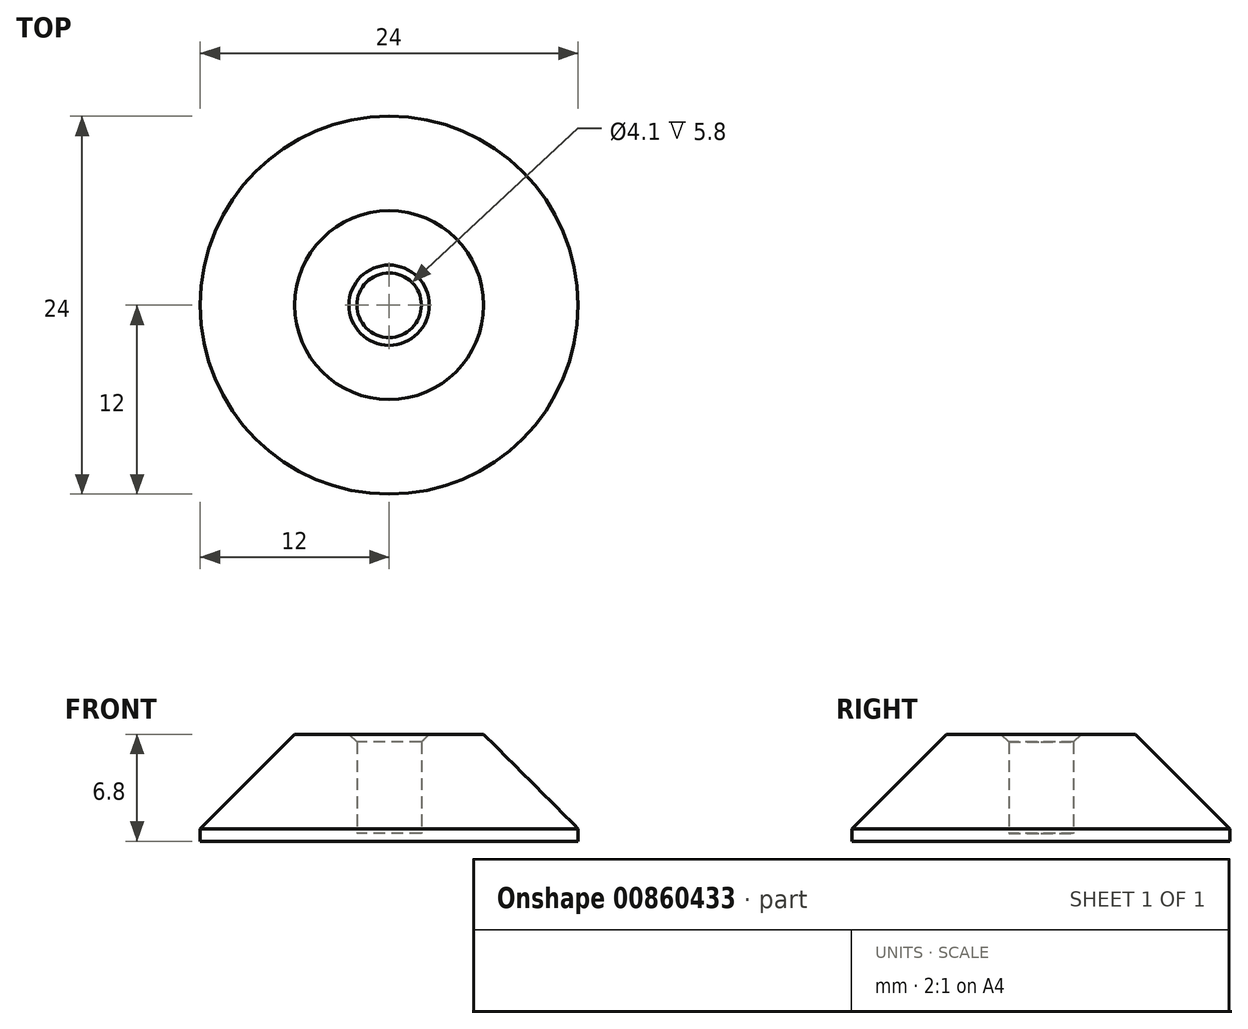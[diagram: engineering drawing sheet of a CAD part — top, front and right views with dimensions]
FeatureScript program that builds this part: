
annotation { "Feature Type Name" : "Feature", "Feature Type Description" : "" }
export const myFeature = defineFeature(function(context is Context, id is Id, definition is map)
    precondition{}
    {
        {
            var Q0;
            Q0=qCreatedBy(makeId("Top.planeOp"),FACE);
            var sketch = newSketch(context, id + "F0", { "sketchPlane" : qUnion([Q0])});
            skCircle(sketch, "E0", {"center": v(0, 0) * mm, "radius": 12 * mm});
            skCircle(sketch, "E1", {"center": v(0, 0) * mm, "radius": 2.05 * mm});
            skSolve(sketch);
        }
        {
            var Q0;
            Q0=makeQuery(id+"F0.imprint","IMPRINT",FACE,{"disambiguationData":[TD([[makeQuery(id+"F0.imprint","IMPRINT",EDGE,{"derivedFrom":sQuery(id+"F0.wireOp",EDGE,"E0")}),1.0]])]});
            extrude(context, id + "F1", {"entities" : qUnion([Q0]), "depth" : 6.8 * mm, "offsetDistance" : 25 * mm});
        }
        {
            var Q0;
            Q0=makeQuery(id+"F0.imprint","IMPRINT",FACE,{"disambiguationData":[TD([[makeQuery(id+"F0.imprint","IMPRINT",EDGE,{"derivedFrom":sQuery(id+"F0.wireOp",EDGE,"E1")}),1.0]])]});
            extrude(context, id + "F2", {"entities" : qUnion([Q0]), "operationType" : NewBodyOperationType.ADD, "depth" : 0.5 * mm, "offsetDistance" : 25 * mm});
        }
        {
            var Q0;
            Q0=makeQuery(id+"F1.opExtrude","CAP_EDGE",EDGE,{"disambiguationData":[OSD([sQuery(id+"F0.wireOp",EDGE,"E1")])],"isStart":false});
            chamfer(context, id + "F3", {"entities" : qUnion([Q0]), "width" : 0.5 * mm, "tangentPropagation" : true});
        }
        {
            var Q0;
            Q0=makeQuery(id+"F1.opExtrude","CAP_EDGE",EDGE,{"disambiguationData":[OSD([sQuery(id+"F0.wireOp",EDGE,"E0")])],"isStart":false});
            chamfer(context, id + "F4", {"entities" : qUnion([Q0]), "width" : 6 * mm, "tangentPropagation" : true});
        }
    });
